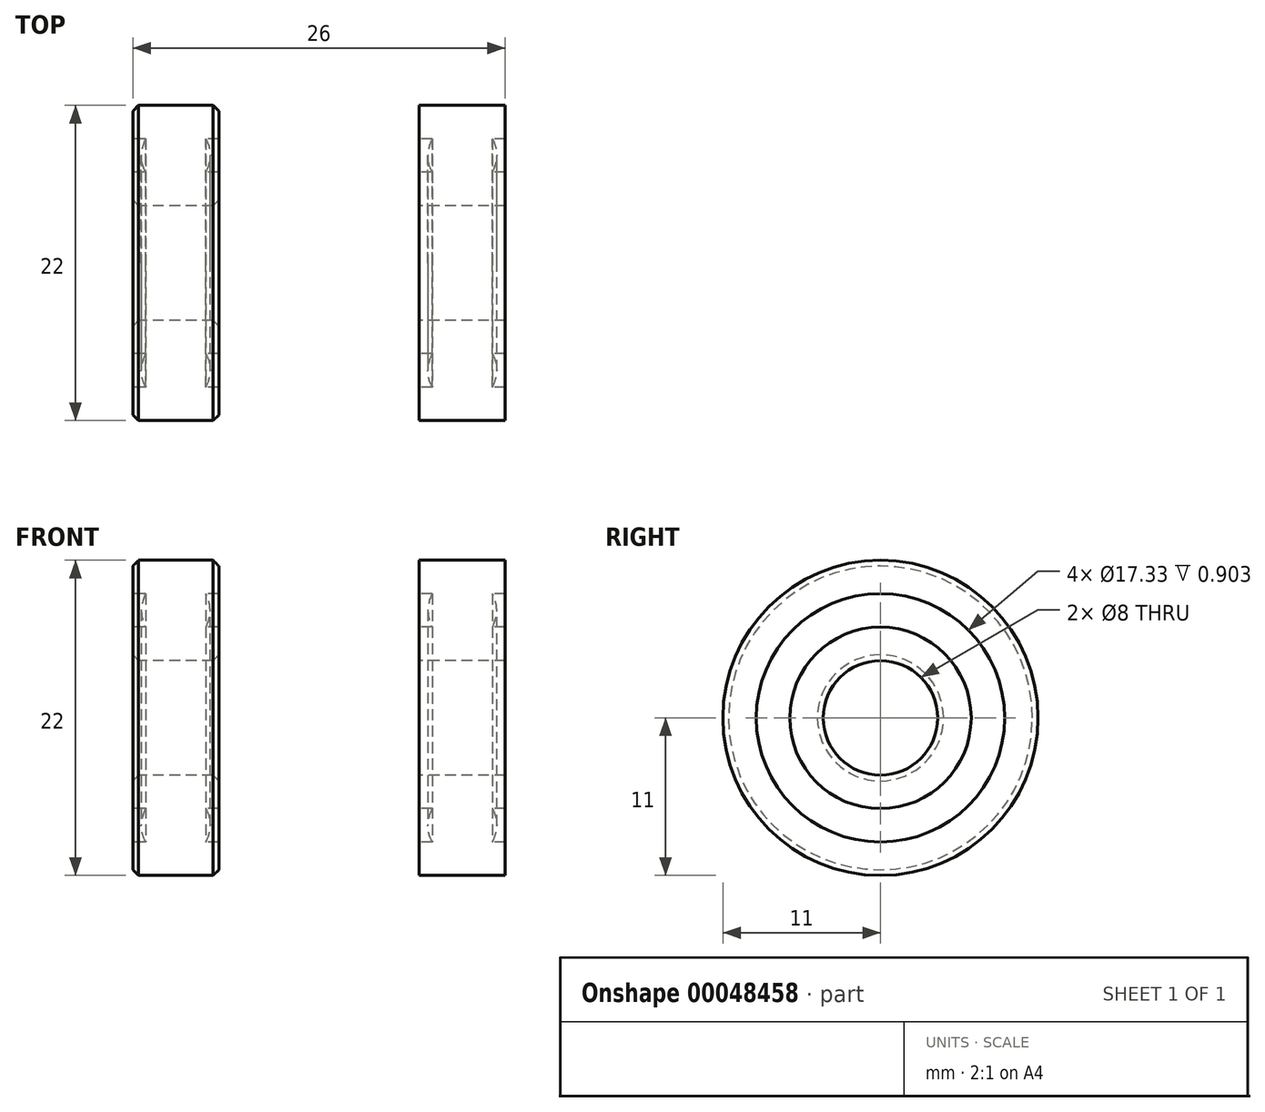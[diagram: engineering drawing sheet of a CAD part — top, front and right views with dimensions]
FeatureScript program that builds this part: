
annotation { "Feature Type Name" : "Feature", "Feature Type Description" : "" }
export const myFeature = defineFeature(function(context is Context, id is Id, definition is map)
    precondition{}
    {
        {
            assignVariable(context, id + "F0", {"name" : "W", "anyValue" : 6});
        }
        {
            var Q0;
            Q0=qCreatedBy(makeId("Front.planeOp"),FACE);
            var sketch = newSketch(context, id + "F1", { "sketchPlane" : qUnion([Q0])});
            skLineSegment(sketch, "E0.rect.bottom", {"start": v(3, 8.67) * mm, "end": v(2.1, 8.67) * mm});
            skLineSegment(sketch, "E0.rect.top", {"start": v(3, 11) * mm, "end": v(-3, 11) * mm});
            skLineSegment(sketch, "E0.rect.left", {"start": v(3, 8.67) * mm, "end": v(3, 11) * mm});
            skLineSegment(sketch, "E0.rect.right", {"start": v(-3, 8.67) * mm, "end": v(-3, 11) * mm});
            skPoint(sketch, "E0.rect.middle", {"position": v(0, 9.83) * mm});
            skLineSegment(sketch, "E1.rect.bottom", {"start": v(-3, 6.33) * mm, "end": v(-2.1, 6.33) * mm});
            skLineSegment(sketch, "E1.rect.top", {"start": v(-3, 4) * mm, "end": v(3, 4) * mm});
            skLineSegment(sketch, "E1.rect.left", {"start": v(-3, 6.33) * mm, "end": v(-3, 4) * mm});
            skLineSegment(sketch, "E1.rect.right", {"start": v(3, 6.33) * mm, "end": v(3, 4) * mm});
            skPoint(sketch, "E1.rect.middle", {"position": v(0, 5.17) * mm});
            skLineSegment(sketch, "E2", {"start": v(0, 8.67) * mm, "end": v(0, 6.33) * mm, "construction": true});
            skLineSegment(sketch, "E3", {"start": v(0, 7.5) * mm, "end": v(2, 7.5) * mm, "construction": true});
            skArc(sketch, "E4", {"start": v(-2.1, 8.67) * mm, "mid": v(-2.4, 7.5) * mm, "end": v(-2.1, 6.33) * mm});
            skLineSegment(sketch, "E5.trimOffspring", {"start": v(-2.1, 8.67) * mm, "end": v(-3, 8.67) * mm});
            skLineSegment(sketch, "E6.trimOffspring", {"start": v(2.1, 6.33) * mm, "end": v(3, 6.33) * mm});
            skArc(sketch, "E7.trimOffspring", {"start": v(2.1, 6.33) * mm, "mid": v(2.4, 7.5) * mm, "end": v(2.1, 8.67) * mm});
            skLineSegment(sketch, "E8", {"start": v(0, 0) * mm, "end": v(37.66, 0) * mm, "construction": true});
            skSolve(sketch);
        }
        {
            var Q0;
            Q0=makeQuery(id+"F1.imprint","IMPRINT",FACE,{"disambiguationData":[TD([[makeQuery(id+"F1.imprint","IMPRINT",EDGE,{"derivedFrom":sQuery(id+"F1.wireOp",EDGE,"E0.rect.bottom")}),-1.0]])]});
            var Q1;
            Q1=sQuery(id+"F1.wireOp",EDGE,"E8");
            revolve(context, id + "F2", {"entities" : qUnion([Q0]), "axis" : qUnion([Q1]), "revolveType" : RevolveType.FULL});
        }
        {
            var Q0;
            Q0=makeQuery(id+"F2.opRevolve","SWEPT_BODY",BODY,{"disambiguationData":[OSD([sQuery(id+"F1.wireOp",EDGE,"E0.rect.bottom"),sQuery(id+"F1.wireOp",EDGE,"E0.rect.top"),sQuery(id+"F1.wireOp",EDGE,"E0.rect.left"),sQuery(id+"F1.wireOp",EDGE,"E0.rect.right"),sQuery(id+"F1.wireOp",EDGE,"E1.rect.bottom"),sQuery(id+"F1.wireOp",EDGE,"E1.rect.top"),sQuery(id+"F1.wireOp",EDGE,"E1.rect.left"),sQuery(id+"F1.wireOp",EDGE,"E1.rect.right"),sQuery(id+"F1.wireOp",EDGE,"E4"),sQuery(id+"F1.wireOp",EDGE,"E5.trimOffspring"),sQuery(id+"F1.wireOp",EDGE,"E6.trimOffspring"),sQuery(id+"F1.wireOp",EDGE,"E7.trimOffspring")])]});
            transform(context, id + "F3", {"entities" : qUnion([Q0]), "transformType" : TransformType.TRANSLATION_3D, "dx" : 20 * mm, "dy" : 0 * mm, "dz" : 0 * mm, "makeCopy" : true});
        }
        {
            var Q0;
            Q0=makeQuery(id+"F2.opRevolve","SWEPT_EDGE",EDGE,{"disambiguationData":[OSD([sQuery(id+"F1.wireOp",EDGE,"E0.rect.top"),sQuery(id+"F1.wireOp",EDGE,"E0.rect.right")])]});
            var Q1;
            Q1=makeQuery(id+"F2.opRevolve","SWEPT_EDGE",EDGE,{"disambiguationData":[OSD([sQuery(id+"F1.wireOp",EDGE,"E0.rect.top"),sQuery(id+"F1.wireOp",EDGE,"E0.rect.left")])]});
            var Q2;
            Q2=makeQuery(id+"F2.opRevolve","SWEPT_EDGE",EDGE,{"disambiguationData":[OSD([sQuery(id+"F1.wireOp",EDGE,"E1.rect.top"),sQuery(id+"F1.wireOp",EDGE,"E1.rect.right")])]});
            var Q3;
            Q3=makeQuery(id+"F2.opRevolve","SWEPT_EDGE",EDGE,{"disambiguationData":[OSD([sQuery(id+"F1.wireOp",EDGE,"E1.rect.top"),sQuery(id+"F1.wireOp",EDGE,"E1.rect.left")])]});
            chamfer(context, id + "F4", {"entities" : qUnion([Q0, Q1, Q2, Q3]), "width" : (getVariable(context, 'W') / 15) * mm, "tangentPropagation" : true});
        }
    });
